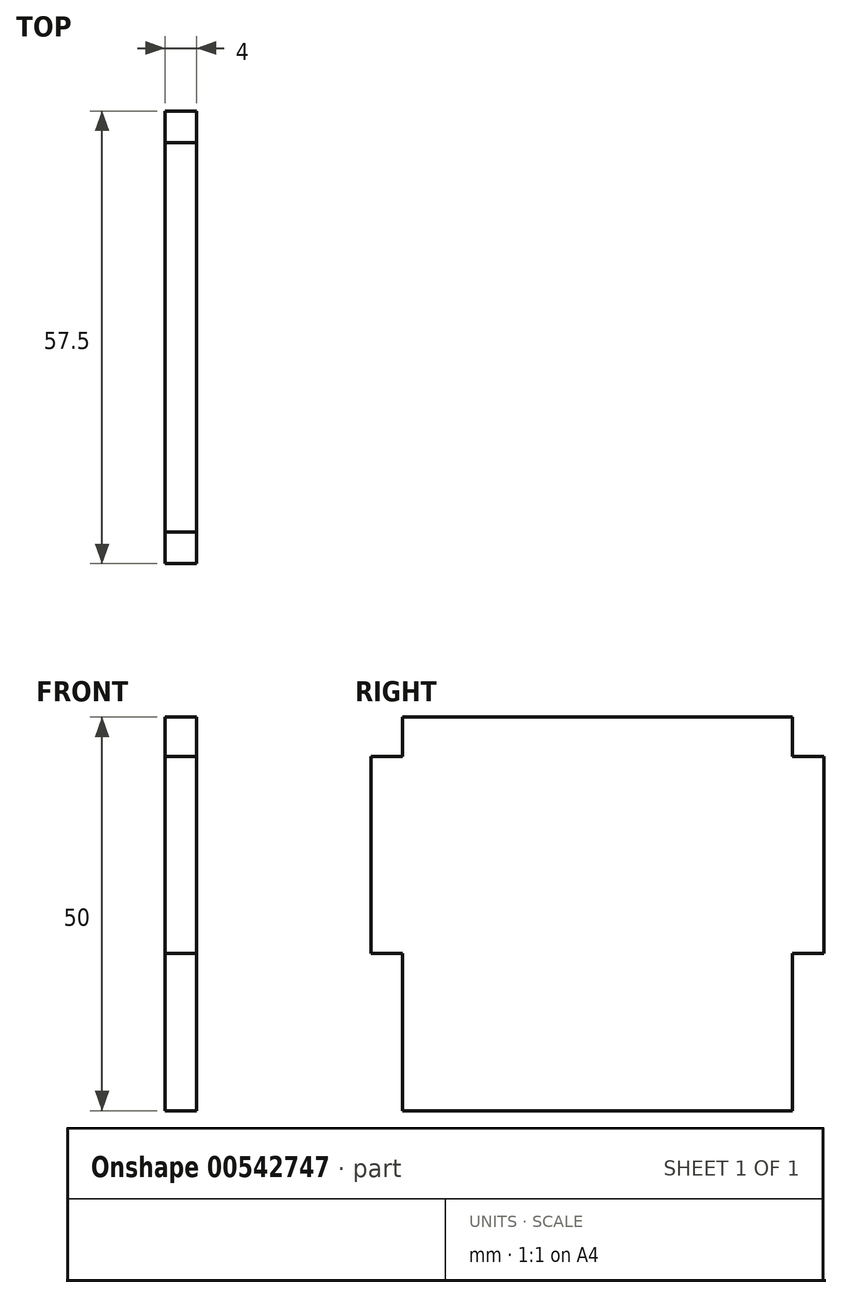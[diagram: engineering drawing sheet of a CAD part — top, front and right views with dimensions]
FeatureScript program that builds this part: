
annotation { "Feature Type Name" : "Feature", "Feature Type Description" : "" }
export const myFeature = defineFeature(function(context is Context, id is Id, definition is map)
    precondition{}
    {
        {
            var Q0;
            Q0=qCreatedBy(makeId("Right.planeOp"),FACE);
            var sketch = newSketch(context, id + "F0", { "sketchPlane" : qUnion([Q0])});
            skLineSegment(sketch, "E0.top", {"start": v(-24.5, -45) * mm, "end": v(25, -45) * mm});
            skLineSegment(sketch, "E1.bottom", {"start": v(-24.5, 0) * mm, "end": v(-28.5, 0) * mm});
            skLineSegment(sketch, "E1.top", {"start": v(-24.5, -25) * mm, "end": v(-28.5, -25) * mm});
            skLineSegment(sketch, "E1.right", {"start": v(-28.5, 0) * mm, "end": v(-28.5, -25) * mm});
            skLineSegment(sketch, "E2.bottom", {"start": v(25, 0) * mm, "end": v(29, 0) * mm});
            skLineSegment(sketch, "E2.top", {"start": v(25, -25) * mm, "end": v(29, -25) * mm});
            skLineSegment(sketch, "E2.right", {"start": v(29, 0) * mm, "end": v(29, -25) * mm});
            skLineSegment(sketch, "E3.trimOffspring", {"start": v(-24.5, 5) * mm, "end": v(-24.5, 0) * mm});
            skLineSegment(sketch, "E4.trimOffspring", {"start": v(-24.5, -25) * mm, "end": v(-24.5, -45) * mm});
            skLineSegment(sketch, "E5.trimOffspring", {"start": v(25, 5) * mm, "end": v(25, 0) * mm});
            skLineSegment(sketch, "E6.trimOffspring", {"start": v(25, -25) * mm, "end": v(25, -45) * mm});
            skLineSegment(sketch, "E7", {"start": v(-24.5, 5) * mm, "end": v(25, 5) * mm});
            skSolve(sketch);
        }
        {
            var Q0;
            Q0 = qSketchRegion(id + "F0", true);
            extrude(context, id + "F1", {"entities" : qUnion([Q0]), "depth" : 4 * mm, "offsetDistance" : 25 * mm});
        }
    });
